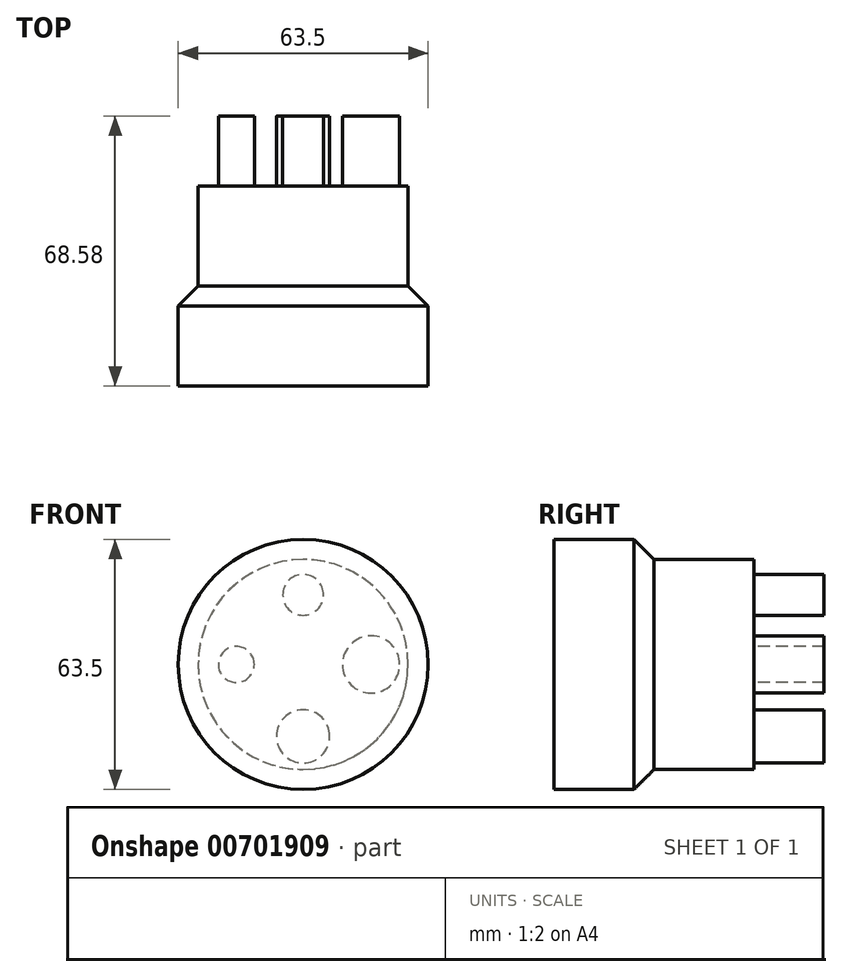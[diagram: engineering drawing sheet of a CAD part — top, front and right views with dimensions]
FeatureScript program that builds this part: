
annotation { "Feature Type Name" : "Feature", "Feature Type Description" : "" }
export const myFeature = defineFeature(function(context is Context, id is Id, definition is map)
    precondition{}
    {
        {
            var Q0;
            Q0=qCreatedBy(makeId("Front.planeOp"),FACE);
            var sketch = newSketch(context, id + "F0", { "sketchPlane" : qUnion([Q0])});
            skCircle(sketch, "E0", {"center": v(0, 0) * mm, "radius": 31.75 * mm});
            skSolve(sketch);
        }
        {
            var Q0;
            Q0=makeQuery(id+"F0.imprint","IMPRINT",FACE,{"disambiguationData":[TD([[makeQuery(id+"F0.imprint","IMPRINT",EDGE,{"derivedFrom":sQuery(id+"F0.wireOp",EDGE,"E0")}),1.0]])]});
            extrude(context, id + "F1", {"entities" : qUnion([Q0]), "depth" : 25.4 * mm, "offsetDistance" : 25.4 * mm});
        }
        {
            var Q0;
            Q0=makeQuery(id+"F1.opExtrude","CAP_FACE",FACE,{"disambiguationData":[OSD([sQuery(id+"F0.wireOp",EDGE,"E0")])],"isStart":true});
            var sketch = newSketch(context, id + "F2", { "sketchPlane" : qUnion([Q0])});
            skSolve(sketch);
        }
        {
            var Q0;
            Q0=makeQuery(id+"F1.opExtrude","CAP_EDGE",EDGE,{"disambiguationData":[OSD([sQuery(id+"F0.wireOp",EDGE,"E0")])],"isStart":true});
            chamfer(context, id + "F3", {"entities" : qUnion([Q0]), "width" : 5.08 * mm, "tangentPropagation" : true});
        }
        {
            var Q0;
            Q0=makeQuery(id+"F2.imprint","IMPRINT",FACE,{"disambiguationData":[TD([[makeQuery(id+"F2.imprint","IMPRINT",EDGE,{"derivedFrom":makeQuery(id+"F1.opExtrude","CAP_EDGE",EDGE,{"disambiguationData":[OSD([sQuery(id+"F0.wireOp",EDGE,"E0")])],"isStart":true})}),-1.0]])]});
            var sketch = newSketch(context, id + "F4", { "sketchPlane" : qUnion([Q0])});
            skCircle(sketch, "E1.0", {"center": v(0, 0) * mm, "radius": 26.67 * mm});
            skSolve(sketch);
        }
        {
            var Q0;
            Q0 = qSketchRegion(id + "F4", true);
            extrude(context, id + "F5", {"entities" : qUnion([Q0]), "operationType" : NewBodyOperationType.ADD, "depth" : 25.4 * mm, "offsetDistance" : 25.4 * mm});
        }
        {
            var Q0;
            Q0=makeQuery(id+"F5.opExtrude","CAP_FACE",FACE,{"disambiguationData":[OSD([sQuery(id+"F4.wireOp",EDGE,"E1.0")])],"isStart":false});
            var sketch = newSketch(context, id + "F6", { "sketchPlane" : qUnion([Q0])});
            skCircle(sketch, "E2", {"center": v(0, 17.68) * mm, "radius": 5.2 * mm});
            skCircle(sketch, "E3", {"center": v(-17.26, 0) * mm, "radius": 7.27 * mm});
            skCircle(sketch, "E4", {"center": v(0, -18.26) * mm, "radius": 6.76 * mm});
            skCircle(sketch, "E5", {"center": v(16.97, 0) * mm, "radius": 4.56 * mm});
            skSolve(sketch);
        }
        {
            var Q0;
            Q0 = qSketchRegion(id + "F6", true);
            extrude(context, id + "F7", {"entities" : qUnion([Q0]), "operationType" : NewBodyOperationType.ADD, "depth" : 17.78 * mm, "offsetDistance" : 25.4 * mm});
        }
    });
